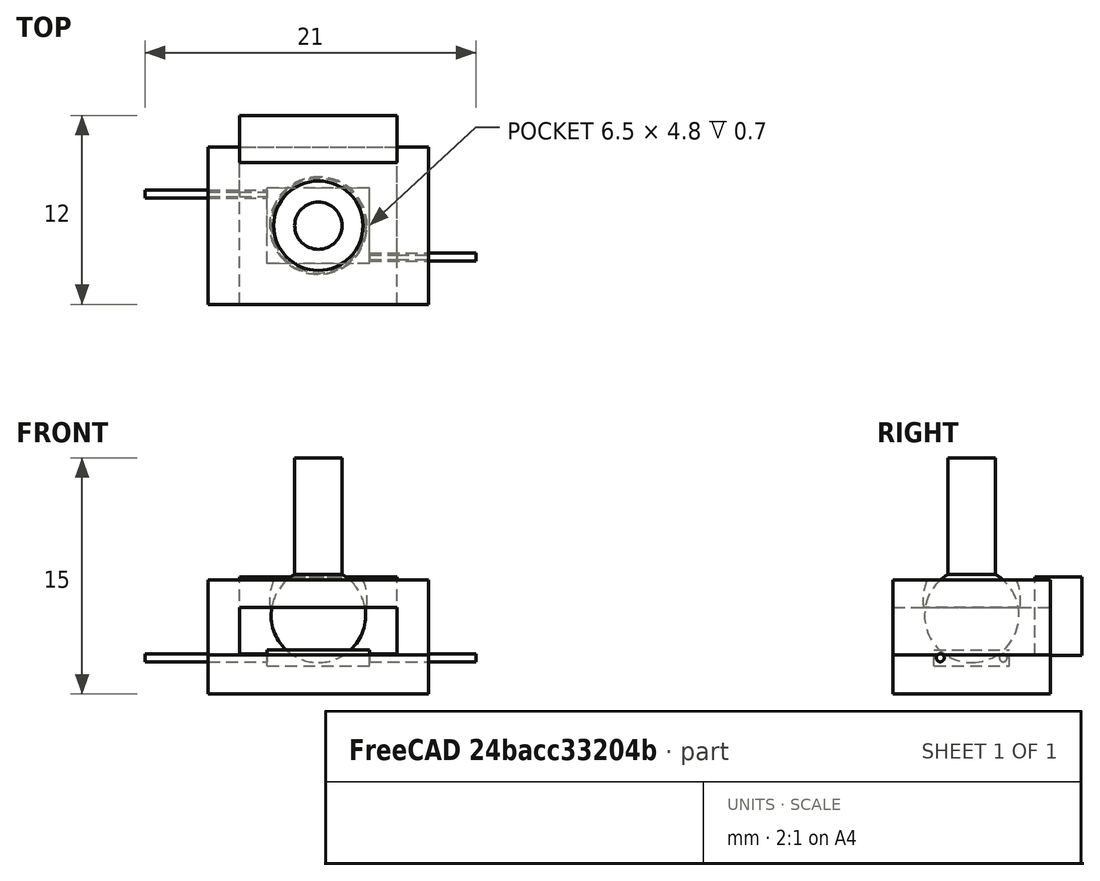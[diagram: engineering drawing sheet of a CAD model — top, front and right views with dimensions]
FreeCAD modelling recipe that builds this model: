
FCSTD DOCUMENT  (FreeCAD 0.16R6710 (Git))
Label: Feet sensors0.2
License: All rights reserved
LicenseURL: http://en.wikipedia.org/wiki/All_rights_reserved
objects: Part::Box×7, Part::Cylinder×6, Part::Fuse×6, Part::Cut×5, Part::Sphere×2, Part::MultiCommon×1
note: 27 computed .brp shape members not serialized (recipe doc carries the construction recipe); baked Part::Feature solids carry a one-line shape summary decoded from their .brp

FEATURE [Part::Sphere] Sphere
  Angle1 = -90
  Angle2 = 90
  Angle3 = 360
  Radius = 3
FEATURE [Part::Cylinder] Cylinder
  Angle = 360
  Height = 10
  Radius = 1.5
FEATURE [Part::Box] Box  label="Cube"
  Height = 1
  Length = 6.5
  Placement = pos=(-3.25,-2.4,-4.2) rot=(0,0,1;0rad)
  Width = 4.8
FEATURE [Part::Cylinder] Cylinder001
  Angle = 360
  Height = 10
  Placement = pos=(-11,2,-3.7) rot=(0,1,0;1.5708rad)
  Radius = 0.25
FEATURE [Part::Cylinder] Cylinder002
  Angle = 360
  Height = 10
  Placement = pos=(0,-2,-3.7) rot=(0,1,0;1.5708rad)
  Radius = 0.25
FEATURE [Part::Box] Box001  label="Cube001"
  Height = 7.25
  Length = 14
  Placement = pos=(-7,-5,-6) rot=(0,0,1;0rad)
  Width = 10
FEATURE [Part::Box] Box002  label="Cube002"
  Height = 1
  Length = 6.5
  Placement = pos=(-3.25,-2.4,-4.2) rot=(0,0,1;0rad)
  Width = 4.8
FEATURE [Part::Cylinder] Cylinder003
  Angle = 360
  Height = 10
  Placement = pos=(-11,2,-3.7) rot=(0,1,0;1.5708rad)
  Radius = 0.25
FEATURE [Part::Cylinder] Cylinder004
  Angle = 360
  Height = 10
  Placement = pos=(0,-2,-3.7) rot=(0,1,0;1.5708rad)
  Radius = 0.25
FEATURE [Part::Fuse] Fusion
  Base = -> Cylinder003
  Tool = -> Cylinder004
FEATURE [Part::Fuse] Fusion001
  Base = -> Box002
  Tool = -> Fusion
FEATURE [Part::Box] Box003  label="Cube003"
  Height = 3
  Length = 10
  Placement = pos=(-5,-6,-3.5) rot=(0,0,1;0rad)
  Width = 12
FEATURE [Part::Cut] Cut
  Base = -> Box001
  Tool = -> Box003
FEATURE [Part::Cut] Cut001
  Base = -> Cut
  Tool = -> Fusion001
FEATURE [Part::Fuse] Fusion002
  Base = -> Cylinder001
  Tool = -> Cylinder002
FEATURE [Part::Fuse] Fusion003  label="Switch"
  Base = -> Box
  Tool = -> Fusion002
FEATURE [Part::Box] Box004  label="Cube004"
  Height = 5
  Length = 10
  Placement = pos=(-5,4,-3.55) rot=(0,0,1;0rad)
  Width = 3
FEATURE [Part::Sphere] Sphere001
  Angle1 = -90
  Angle2 = 90
  Angle3 = 360
  Radius = 3.1
FEATURE [Part::Cylinder] Cylinder005
  Angle = 360
  Height = 10
  Placement = pos=(0,0,0.5) rot=(0,0,1;0rad)
  Radius = 2.5
FEATURE [Part::Fuse] Fusion004
  Base = -> Sphere001
  Tool = -> Cylinder005
FEATURE [Part::Cut] Cut002
  Base = -> Cut001
  Tool = -> Fusion004
FEATURE [Part::Fuse] Fusion005  label="Ball and Screw"
  Base = -> Sphere
  Placement = pos=(0,0,-1) rot=(0,0,1;0rad)
  Tool = -> Cylinder
FEATURE [Part::Cut] Cut003
  Base = -> Cut001
  Tool = -> Fusion004
FEATURE [Part::Box] Box005  label="Cube005"
  Height = 8
  Length = 21
  Placement = pos=(-9,-7,-3.5) rot=(0,0,1;0rad)
  Width = 17
FEATURE [Part::Box] Box006  label="Cube006"
  Height = 12
  Length = 21
  Placement = pos=(-9,-7,-3.5) rot=(0,0,1;0rad)
  Width = 17
FEATURE [Part::Cut] Cut004  label="Bottom Switch holder"
  Base = -> Cut003
  Tool = -> Box005
FEATURE [Part::MultiCommon] Common  label="Ball and screw holder"
  Shapes = -> [Cut002,Box006]
